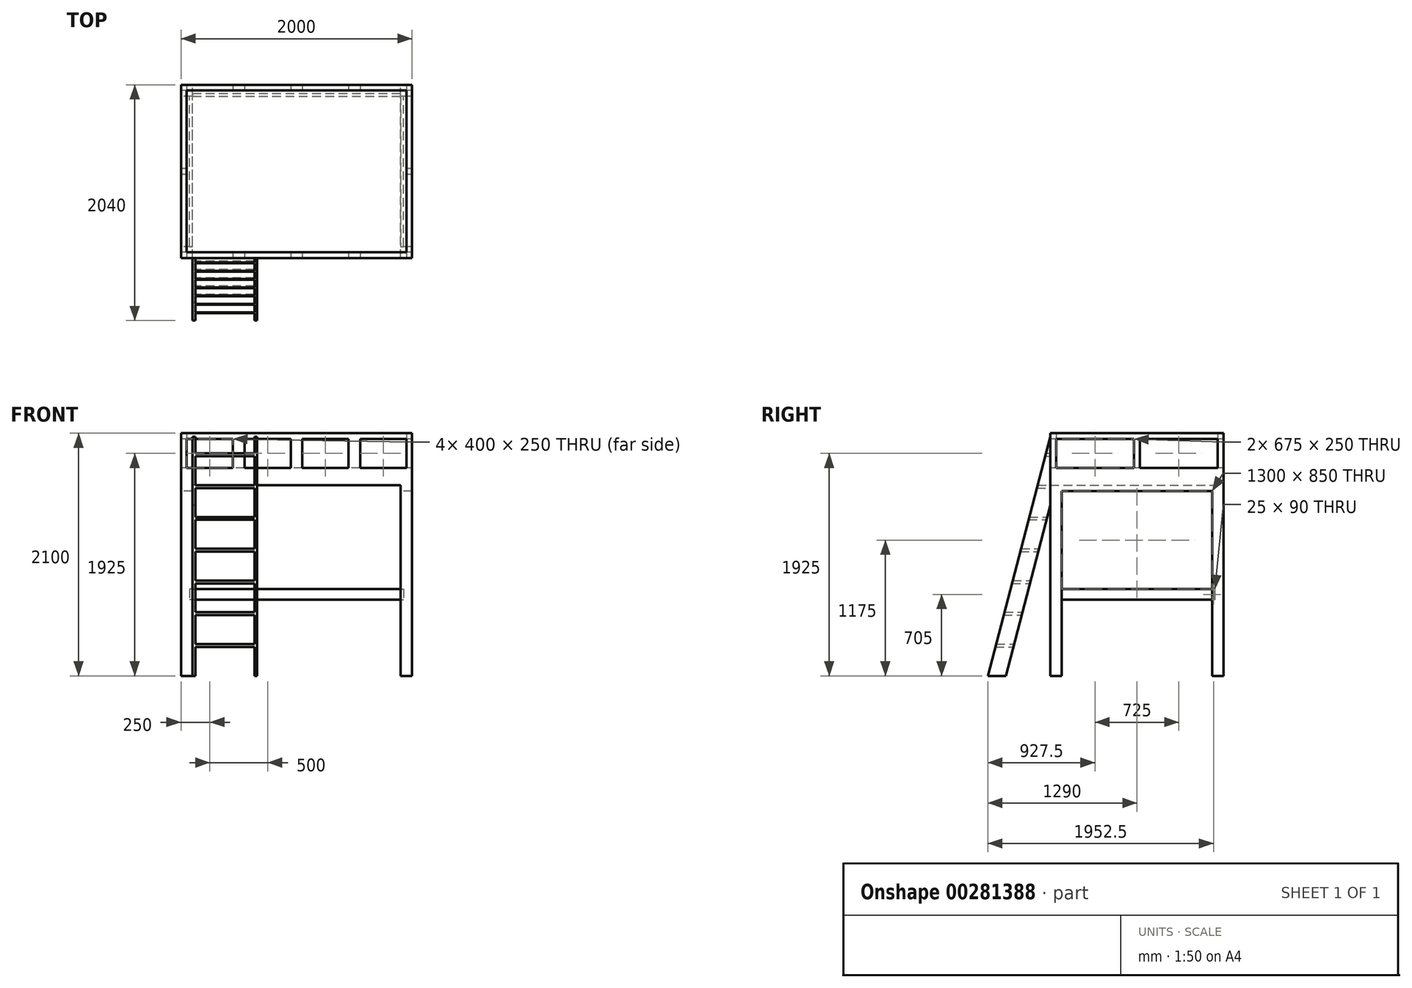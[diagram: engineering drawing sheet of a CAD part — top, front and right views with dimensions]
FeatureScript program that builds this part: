
annotation { "Feature Type Name" : "Feature", "Feature Type Description" : "" }
export const myFeature = defineFeature(function(context is Context, id is Id, definition is map)
    precondition{}
    {
        {
            var Q0;
            Q0=qCreatedBy(makeId("Front.planeOp"),FACE);
            var sketch = newSketch(context, id + "F0", { "sketchPlane" : qUnion([Q0])});
            skLineSegment(sketch, "E0", {"start": v(-1000, 0) * mm, "end": v(-1000, 1800) * mm});
            skLineSegment(sketch, "E1", {"start": v(-1000, 1800) * mm, "end": v(0, 1800) * mm});
            skLineSegment(sketch, "E2", {"start": v(0, 1800) * mm, "end": v(0, -22.44) * mm, "construction": true});
            skLineSegment(sketch, "E3", {"start": v(0, 1800) * mm, "end": v(0, 1650) * mm});
            skLineSegment(sketch, "E4", {"start": v(0, 1650) * mm, "end": v(-900, 1650) * mm});
            skLineSegment(sketch, "E5", {"start": v(-900, 1650) * mm, "end": v(-900, 0) * mm});
            skLineSegment(sketch, "E6", {"start": v(-900, 0) * mm, "end": v(-1000, 0) * mm});
            skSolve(sketch);
        }
        {
            var Q0;
            Q0=qSketchRegion(id+"F0",true);
            extrude(context, id + "F1", {"entities" : qUnion([Q0]), "depth" : 1500 * mm});
        }
        {
            var Q0;
            Q0=makeQuery(id+"F1.opExtrude","SWEPT_BODY",BODY,{"disambiguationData":[OSD([sQuery(id+"F0.wireOp",EDGE,"E0"),sQuery(id+"F0.wireOp",EDGE,"E1"),sQuery(id+"F0.wireOp",EDGE,"E3"),sQuery(id+"F0.wireOp",EDGE,"E4"),sQuery(id+"F0.wireOp",EDGE,"E5"),sQuery(id+"F0.wireOp",EDGE,"E6")])]});
            var Q1;
            Q1=qCreatedBy(makeId("Right.planeOp"),FACE);
            mirror(context, id + "F2", {"operationType" : NewBodyOperationType.ADD, "entities" : qUnion([Q0]), "mirrorPlane" : qUnion([Q1])});
        }
        {
            var Q0;
            {var subQ0=makeQuery(id+"F1.opExtrude","SWEPT_FACE",FACE,{"disambiguationData":[OSD([sQuery(id+"F0.wireOp",EDGE,"E1")])]});Q0=makeQuery(id+"F2.boolean.opBoolean","MERGE",FACE,{"derivedFrom":[subQ0,makeQuery(id+"F2.opPattern","COPY",FACE,{"derivedFrom":subQ0,"instanceName":"1"})]});}
            var sketch = newSketch(context, id + "F3", { "sketchPlane" : qUnion([Q0])});
            skLineSegment(sketch, "E7.bottom", {"start": v(1000, -1500) * mm, "end": v(-1000, -1500) * mm});
            skLineSegment(sketch, "E7.top", {"start": v(1000, 0) * mm, "end": v(-1000, 0) * mm});
            skLineSegment(sketch, "E7.left", {"start": v(1000, -1500) * mm, "end": v(1000, -1450) * mm});
            skLineSegment(sketch, "E7.right", {"start": v(-1000, -1500) * mm, "end": v(-1000, -50) * mm});
            skLineSegment(sketch, "E8", {"start": v(950, -50) * mm, "end": v(-950, -50) * mm});
            skLineSegment(sketch, "E9", {"start": v(-950, -50) * mm, "end": v(-950, -1450) * mm});
            skLineSegment(sketch, "E10", {"start": v(-950, -1450) * mm, "end": v(950, -1450) * mm});
            skLineSegment(sketch, "E11.trimOffspring", {"start": v(-1000, -50) * mm, "end": v(-1000, 0) * mm});
            skLineSegment(sketch, "E12", {"start": v(950, -50) * mm, "end": v(950, -1450) * mm});
            skLineSegment(sketch, "E13", {"start": v(1000, -1450) * mm, "end": v(1000, 0) * mm});
            skSolve(sketch);
        }
        {
            var Q0;
            Q0=qSketchRegion(id+"F3",true);
            extrude(context, id + "F4", {"entities" : qUnion([Q0]), "operationType" : NewBodyOperationType.ADD, "depth" : 300 * mm});
        }
        {
            var Q0;
            {var subQ0=makeQuery(id+"F1.opExtrude","CAP_FACE",FACE,{"disambiguationData":[OSD([sQuery(id+"F0.wireOp",EDGE,"E0"),sQuery(id+"F0.wireOp",EDGE,"E1"),sQuery(id+"F0.wireOp",EDGE,"E3"),sQuery(id+"F0.wireOp",EDGE,"E4"),sQuery(id+"F0.wireOp",EDGE,"E5"),sQuery(id+"F0.wireOp",EDGE,"E6")])],"isStart":false});Q0=makeQuery(id+"F4.boolean.opBoolean","MERGE",FACE,{"derivedFrom":[makeQuery(id+"F2.boolean.opBoolean","MERGE",FACE,{"derivedFrom":[subQ0,makeQuery(id+"F2.opPattern","COPY",FACE,{"derivedFrom":subQ0,"instanceName":"1"})]}),makeQuery(id+"F4.opExtrude","SWEPT_FACE",FACE,{"disambiguationData":[OSD([sQuery(id+"F3.wireOp",EDGE,"E7.bottom")])]})]});}
            var sketch = newSketch(context, id + "F5", { "sketchPlane" : qUnion([Q0])});
            skLineSegment(sketch, "E14.bottom", {"start": v(-950, 2050) * mm, "end": v(-550, 2050) * mm});
            skLineSegment(sketch, "E14.top", {"start": v(-950, 1800) * mm, "end": v(-550, 1800) * mm});
            skLineSegment(sketch, "E14.left", {"start": v(-950, 2050) * mm, "end": v(-950, 1800) * mm});
            skLineSegment(sketch, "E14.right", {"start": v(-550, 2050) * mm, "end": v(-550, 1800) * mm});
            skLineSegment(sketch, "E15.1.0.0", {"start": v(-450, 2050) * mm, "end": v(-450, 1800) * mm});
            skLineSegment(sketch, "E15.1.0.1", {"start": v(-450, 2050) * mm, "end": v(-50, 2050) * mm});
            skLineSegment(sketch, "E15.1.0.2", {"start": v(-50, 2050) * mm, "end": v(-50, 1800) * mm});
            skLineSegment(sketch, "E15.1.0.3", {"start": v(-450, 1800) * mm, "end": v(-50, 1800) * mm});
            skLineSegment(sketch, "E15.2.0.0", {"start": v(50, 2050) * mm, "end": v(50, 1800) * mm});
            skLineSegment(sketch, "E15.2.0.1", {"start": v(50, 2050) * mm, "end": v(450, 2050) * mm});
            skLineSegment(sketch, "E15.2.0.2", {"start": v(450, 2050) * mm, "end": v(450, 1800) * mm});
            skLineSegment(sketch, "E15.2.0.3", {"start": v(50, 1800) * mm, "end": v(450, 1800) * mm});
            skLineSegment(sketch, "E15.direction1", {"start": v(-950, 1800) * mm, "end": v(-450, 1800) * mm, "construction": true});
            skLineSegment(sketch, "E16.0.3.0", {"start": v(550, 2050) * mm, "end": v(550, 1800) * mm});
            skLineSegment(sketch, "E16.3.3.0", {"start": v(550, 2050) * mm, "end": v(950, 2050) * mm});
            skLineSegment(sketch, "E16.6.3.0", {"start": v(950, 2050) * mm, "end": v(950, 1800) * mm});
            skLineSegment(sketch, "E16.9.3.0", {"start": v(550, 1800) * mm, "end": v(950, 1800) * mm});
            skLineSegment(sketch, "E17.0.4.0", {"start": v(1050, 2050) * mm, "end": v(1050, 1800) * mm});
            skLineSegment(sketch, "E17.3.4.0", {"start": v(1050, 2050) * mm, "end": v(1450, 2050) * mm});
            skLineSegment(sketch, "E17.6.4.0", {"start": v(1450, 2050) * mm, "end": v(1450, 1800) * mm});
            skLineSegment(sketch, "E17.9.4.0", {"start": v(1050, 1800) * mm, "end": v(1450, 1800) * mm});
            skSolve(sketch);
        }
        {
            var Q0;
            Q0=qSketchRegion(id+"F5",true);
            extrude(context, id + "F6", {"entities" : qUnion([Q0]), "operationType" : NewBodyOperationType.REMOVE, "endBound" : BoundingType.THROUGH_ALL, "oppositeDirection" : true, "depth" : 25 * mm});
        }
        {
            var Q0;
            Q0=makeQuery(id+"F6.boolean.opBoolean","MERGE",FACE,{"derivedFrom":[makeQuery(id+"F4.opExtrude","SWEPT_FACE",FACE,{"disambiguationData":[OSD([sQuery(id+"F3.wireOp",EDGE,"E9")])]}),makeQuery(id+"F6.opExtrude","SWEPT_FACE",FACE,{"disambiguationData":[OSD([sQuery(id+"F5.wireOp",EDGE,"E14.left")])]})]});
            var sketch = newSketch(context, id + "F7", { "sketchPlane" : qUnion([Q0])});
            skLineSegment(sketch, "E18.bottom", {"start": v(-1450, 2050) * mm, "end": v(-775, 2050) * mm});
            skLineSegment(sketch, "E18.top", {"start": v(-1450, 1800) * mm, "end": v(-775, 1800) * mm});
            skLineSegment(sketch, "E18.left", {"start": v(-1450, 2050) * mm, "end": v(-1450, 1800) * mm});
            skLineSegment(sketch, "E18.right", {"start": v(-775, 2050) * mm, "end": v(-775, 1800) * mm});
            skLineSegment(sketch, "E19.1.0.0", {"start": v(-725, 2050) * mm, "end": v(-725, 1800) * mm});
            skLineSegment(sketch, "E19.1.0.1", {"start": v(-725, 2050) * mm, "end": v(-50, 2050) * mm});
            skLineSegment(sketch, "E19.1.0.2", {"start": v(-50, 2050) * mm, "end": v(-50, 1800) * mm});
            skLineSegment(sketch, "E19.1.0.3", {"start": v(-725, 1800) * mm, "end": v(-50, 1800) * mm});
            skLineSegment(sketch, "E19.direction1", {"start": v(-1450, 1800) * mm, "end": v(-725, 1800) * mm, "construction": true});
            skSolve(sketch);
        }
        {
            var Q0;
            Q0=qSketchRegion(id+"F7",true);
            extrude(context, id + "F8", {"entities" : qUnion([Q0]), "operationType" : NewBodyOperationType.REMOVE, "endBound" : BoundingType.THROUGH_ALL, "depth" : 25 * mm, "hasSecondDirection" : true, "secondDirectionBound" : SecondDirectionBoundingType.THROUGH_ALL, "secondDirectionOppositeDirection" : true, "secondDirectionDepth" : 25 * mm});
        }
        {
            var Q0;
            Q0=makeQuery(id+"F4.boolean.opBoolean","MERGE",FACE,{"derivedFrom":[makeQuery(id+"F1.opExtrude","SWEPT_FACE",FACE,{"disambiguationData":[OSD([sQuery(id+"F0.wireOp",EDGE,"E0")])]}),makeQuery(id+"F4.opExtrude","SWEPT_FACE",FACE,{"disambiguationData":[OSD([sQuery(id+"F3.wireOp",EDGE,"E7.right"),sQuery(id+"F3.wireOp",EDGE,"E11.trimOffspring")])]})]});
            var sketch = newSketch(context, id + "F9", { "sketchPlane" : qUnion([Q0])});
            skLineSegment(sketch, "E20.top", {"start": v(100, 1600) * mm, "end": v(1400, 1600) * mm});
            skLineSegment(sketch, "E20.left", {"start": v(100, 0) * mm, "end": v(100, 1600) * mm});
            skLineSegment(sketch, "E20.right", {"start": v(1400, 0) * mm, "end": v(1400, 1600) * mm});
            skLineSegment(sketch, "E21", {"start": v(100, 0) * mm, "end": v(1400, 0) * mm});
            skSolve(sketch);
        }
        {
            var Q0;
            Q0=makeQuery(id+"F9.imprint","IMPRINT",FACE,{"disambiguationData":[TD([[makeQuery(id+"F9.imprint","IMPRINT",EDGE,{"derivedFrom":sQuery(id+"F9.wireOp",EDGE,"E20.top")}),-1.0]])]});
            extrude(context, id + "F10", {"entities" : qUnion([Q0]), "operationType" : NewBodyOperationType.REMOVE, "endBound" : BoundingType.THROUGH_ALL, "oppositeDirection" : true, "depth" : 25 * mm});
        }
        {
            var Q0;
            Q0=qCreatedBy(makeId("Top.planeOp"),FACE);
            cPlane(context, id + "F11", {"entities" : qUnion([Q0]), "cplaneType" : CPlaneType.OFFSET, "offset" : 660 * mm, "width" : 150 * mm, "height" : 150 * mm});
        }
        {
            var Q0;
            Q0=makeQuery(id+"F1.opExtrude","SWEPT_FACE",FACE,{"disambiguationData":[OSD([sQuery(id+"F0.wireOp",EDGE,"E5")])]});
            cPlane(context, id + "F12", {"entities" : qUnion([Q0]), "cplaneType" : CPlaneType.OFFSET, "offset" : 0 * mm, "width" : 150 * mm, "height" : 150 * mm});
        }
        {
            var Q0;
            Q0=qCreatedBy(id+"F12.planeOp",FACE);
            var sketch = newSketch(context, id + "F13", { "sketchPlane" : qUnion([Q0])});
            skLineSegment(sketch, "E22", {"start": v(-1500, 2070) * mm, "end": v(-2040, 0) * mm});
            skLineSegment(sketch, "E23", {"start": v(-2040, 0) * mm, "end": v(-1884.98, 0) * mm});
            skLineSegment(sketch, "E24", {"start": v(-1884.98, 0) * mm, "end": v(-1500, 1475.76) * mm});
            skLineSegment(sketch, "E25", {"start": v(-1500, 1475.76) * mm, "end": v(-1500, 2070) * mm});
            skSolve(sketch);
        }
        {
            var Q0;
            Q0 = qSketchRegion(id + "F13", true);
            extrude(context, id + "F14", {"entities" : qUnion([Q0]), "depth" : 560 * mm});
        }
        {
            var Q0;
            {var subQ0=makeQuery(id+"F1.opExtrude","CAP_FACE",FACE,{"disambiguationData":[OSD([sQuery(id+"F0.wireOp",EDGE,"E0"),sQuery(id+"F0.wireOp",EDGE,"E1"),sQuery(id+"F0.wireOp",EDGE,"E3"),sQuery(id+"F0.wireOp",EDGE,"E4"),sQuery(id+"F0.wireOp",EDGE,"E5"),sQuery(id+"F0.wireOp",EDGE,"E6")])],"isStart":false});Q0=makeQuery(id+"F4.boolean.opBoolean","MERGE",FACE,{"derivedFrom":[makeQuery(id+"F2.boolean.opBoolean","MERGE",FACE,{"derivedFrom":[subQ0,makeQuery(id+"F2.opPattern","COPY",FACE,{"derivedFrom":subQ0,"instanceName":"1"})]}),makeQuery(id+"F4.opExtrude","SWEPT_FACE",FACE,{"disambiguationData":[OSD([sQuery(id+"F3.wireOp",EDGE,"E7.bottom")])]})]});}
            var sketch = newSketch(context, id + "F15", { "sketchPlane" : qUnion([Q0])});
            skLineSegment(sketch, "E26.bottom", {"start": v(-875, 0) * mm, "end": v(-365, 0) * mm});
            skLineSegment(sketch, "E26.top", {"start": v(-875, 250) * mm, "end": v(-365, 250) * mm});
            skLineSegment(sketch, "E26.left", {"start": v(-875, 0) * mm, "end": v(-875, 250) * mm});
            skLineSegment(sketch, "E26.right", {"start": v(-365, 0) * mm, "end": v(-365, 250) * mm});
            skLineSegment(sketch, "E27.0.1.0", {"start": v(-875, 275) * mm, "end": v(-875, 525) * mm});
            skLineSegment(sketch, "E27.0.1.1", {"start": v(-875, 525) * mm, "end": v(-365, 525) * mm});
            skLineSegment(sketch, "E27.0.1.2", {"start": v(-365, 275) * mm, "end": v(-365, 525) * mm});
            skLineSegment(sketch, "E27.0.1.3", {"start": v(-875, 275) * mm, "end": v(-365, 275) * mm});
            skLineSegment(sketch, "E27.0.2.0", {"start": v(-875, 550) * mm, "end": v(-875, 800) * mm});
            skLineSegment(sketch, "E27.0.2.1", {"start": v(-875, 800) * mm, "end": v(-365, 800) * mm});
            skLineSegment(sketch, "E27.0.2.2", {"start": v(-365, 550) * mm, "end": v(-365, 800) * mm});
            skLineSegment(sketch, "E27.0.2.3", {"start": v(-875, 550) * mm, "end": v(-365, 550) * mm});
            skLineSegment(sketch, "E27.0.3.0", {"start": v(-875, 825) * mm, "end": v(-875, 1075) * mm});
            skLineSegment(sketch, "E27.0.3.1", {"start": v(-875, 1075) * mm, "end": v(-365, 1075) * mm});
            skLineSegment(sketch, "E27.0.3.2", {"start": v(-365, 825) * mm, "end": v(-365, 1075) * mm});
            skLineSegment(sketch, "E27.0.3.3", {"start": v(-875, 825) * mm, "end": v(-365, 825) * mm});
            skLineSegment(sketch, "E27.0.4.0", {"start": v(-875, 1100) * mm, "end": v(-875, 1350) * mm});
            skLineSegment(sketch, "E27.0.4.1", {"start": v(-875, 1350) * mm, "end": v(-365, 1350) * mm});
            skLineSegment(sketch, "E27.0.4.2", {"start": v(-365, 1100) * mm, "end": v(-365, 1350) * mm});
            skLineSegment(sketch, "E27.0.4.3", {"start": v(-875, 1100) * mm, "end": v(-365, 1100) * mm});
            skLineSegment(sketch, "E27.0.5.0", {"start": v(-875, 1375) * mm, "end": v(-875, 1625) * mm});
            skLineSegment(sketch, "E27.0.5.1", {"start": v(-875, 1625) * mm, "end": v(-365, 1625) * mm});
            skLineSegment(sketch, "E27.0.5.2", {"start": v(-365, 1375) * mm, "end": v(-365, 1625) * mm});
            skLineSegment(sketch, "E27.0.5.3", {"start": v(-875, 1375) * mm, "end": v(-365, 1375) * mm});
            skLineSegment(sketch, "E27.0.6.0", {"start": v(-875, 1650) * mm, "end": v(-875, 1900) * mm});
            skLineSegment(sketch, "E27.0.6.1", {"start": v(-875, 1900) * mm, "end": v(-365, 1900) * mm});
            skLineSegment(sketch, "E27.0.6.2", {"start": v(-365, 1650) * mm, "end": v(-365, 1900) * mm});
            skLineSegment(sketch, "E27.0.6.3", {"start": v(-875, 1650) * mm, "end": v(-365, 1650) * mm});
            skLineSegment(sketch, "E27.0.7.0", {"start": v(-875, 1925) * mm, "end": v(-875, 2175) * mm});
            skLineSegment(sketch, "E27.0.7.1", {"start": v(-875, 2175) * mm, "end": v(-365, 2175) * mm});
            skLineSegment(sketch, "E27.0.7.2", {"start": v(-365, 1925) * mm, "end": v(-365, 2175) * mm});
            skLineSegment(sketch, "E27.0.7.3", {"start": v(-875, 1925) * mm, "end": v(-365, 1925) * mm});
            skLineSegment(sketch, "E27.direction1", {"start": v(-875, 0) * mm, "end": v(-850, 0) * mm, "construction": true});
            skLineSegment(sketch, "E27.direction2", {"start": v(-875, 0) * mm, "end": v(-875, 275) * mm, "construction": true});
            skSolve(sketch);
        }
        {
            var Q0;
            Q0 = qSketchRegion(id + "F15", true);
            extrude(context, id + "F16", {"entities" : qUnion([Q0]), "operationType" : NewBodyOperationType.REMOVE, "endBound" : BoundingType.THROUGH_ALL, "depth" : 25 * mm});
        }
        {
            var Q0;
            Q0=qCreatedBy(id+"F11.planeOp",FACE);
            var sketch = newSketch(context, id + "F17", { "sketchPlane" : qUnion([Q0])});
            skLineSegment(sketch, "E28.bottom", {"start": v(-925, -1400) * mm, "end": v(-900, -1400) * mm});
            skLineSegment(sketch, "E28.top", {"start": v(-925, -75) * mm, "end": v(925, -75) * mm});
            skLineSegment(sketch, "E28.left", {"start": v(-925, -1400) * mm, "end": v(-925, -75) * mm});
            skLineSegment(sketch, "E28.right", {"start": v(925, -1400) * mm, "end": v(925, -75) * mm});
            skLineSegment(sketch, "E29.top", {"start": v(-900, -100) * mm, "end": v(900, -100) * mm});
            skLineSegment(sketch, "E29.left", {"start": v(-900, -1400) * mm, "end": v(-900, -100) * mm});
            skLineSegment(sketch, "E29.right", {"start": v(900, -1400) * mm, "end": v(900, -100) * mm});
            skLineSegment(sketch, "E30.trimOffspring", {"start": v(900, -1400) * mm, "end": v(925, -1400) * mm});
            skSolve(sketch);
        }
        {
            var Q0;
            Q0 = qSketchRegion(id + "F17", true);
            extrude(context, id + "F18", {"entities" : qUnion([Q0]), "operationType" : NewBodyOperationType.ADD, "depth" : 90 * mm});
        }
    });
